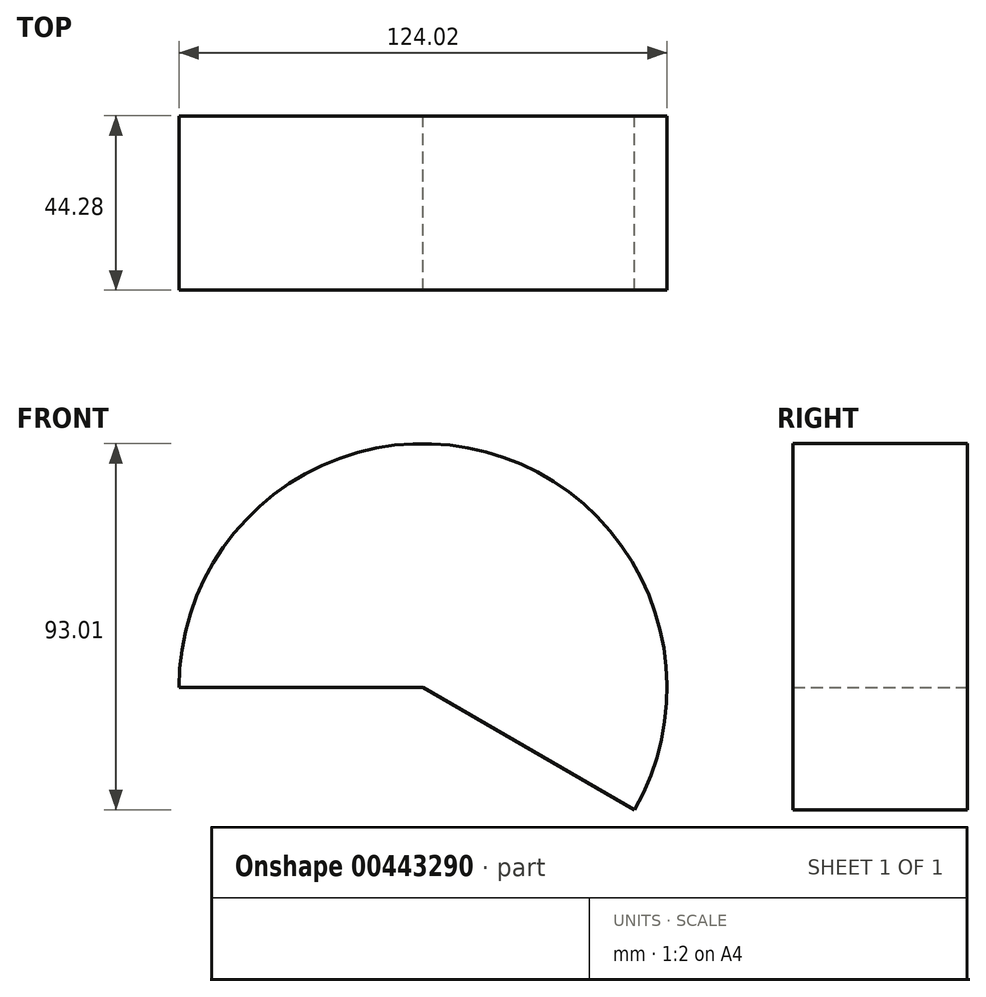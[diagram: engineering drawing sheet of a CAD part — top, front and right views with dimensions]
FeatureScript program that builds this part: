
annotation { "Feature Type Name" : "Feature", "Feature Type Description" : "" }
export const myFeature = defineFeature(function(context is Context, id is Id, definition is map)
    precondition{}
    {
        {
            var Q0;
            Q0=qCreatedBy(makeId("Top.planeOp"),FACE);
            var sketch = newSketch(context, id + "F0", { "sketchPlane" : qUnion([Q0])});
            skLineSegment(sketch, "E0.bottom", {"start": v(-62, 0) * mm, "end": v(0, 0) * mm});
            skLineSegment(sketch, "E0.top", {"start": v(-62, 44.28) * mm, "end": v(0, 44.28) * mm});
            skLineSegment(sketch, "E0.left", {"start": v(-62, 0) * mm, "end": v(-62, 44.28) * mm});
            skLineSegment(sketch, "E0.right", {"start": v(0, 0) * mm, "end": v(0, 44.28) * mm});
            skSolve(sketch);
        }
        {
            var Q0;
            Q0=makeQuery(id+"F0.imprint","IMPRINT",FACE,{"disambiguationData":[TD([[makeQuery(id+"F0.imprint","IMPRINT",EDGE,{"derivedFrom":sQuery(id+"F0.wireOp",EDGE,"E0.bottom")}),1.0]])]});
            var Q1;
            Q1=sQuery(id+"F0.wireOp",EDGE,"E0.right");
            revolve(context, id + "F1", {"entities" : qUnion([Q0]), "axis" : qUnion([Q1]), "revolveType" : RevolveType.ONE_DIRECTION, "angle" : 210 * degree});
        }
    });
